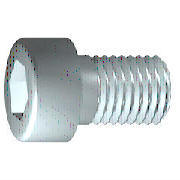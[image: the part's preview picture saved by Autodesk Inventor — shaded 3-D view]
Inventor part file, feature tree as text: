
AUTODESK INVENTOR PART (.ipt)
format: ipt  version: 2023.3 (Build 273359000, 359)  size: 194,048 bytes
history: native  units: mm (DEFAULTED — no unit token found)
features: sketch x2, other x1, extrude x1, plane x1, fillet x1
ambient origin geometry x7: Origin, YZ Plane, XY Plane, X Axis, Y Axis, Z Axis, Center Point
bodies: Solid1 (feature_tree)
feature tree (6):
  other  "Körper"
  extrude  "Loch"  Depth=3.0mm
  plane  "Work Plane1"
  fillet  "Fillet2"  Radius=3.0mm
  sketch  "Skizze1"  dims[d1=6.75mm d2=0.306825mm d3=3.0mm]
  sketch  "Skizze2"  dims[d4=1.3mm d5=60.0deg d6=3.0mm d7=3.0mm d8=2.886751mm d9=5.5mm d10=90.0deg d11=10.0mm d12=0.0mm d13=6.75mm d14=0.0mm d15=0.306725mm d16=0.306725mm d17=0.3mm d19=0.0mm d26=8.0mm d27=45.0deg d28=0.0mm d29=0.0mm d30=0.1mm]
